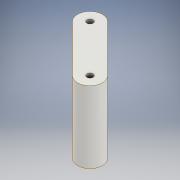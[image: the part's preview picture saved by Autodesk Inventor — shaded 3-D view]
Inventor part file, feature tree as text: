
AUTODESK INVENTOR PART (.ipt)
format: ipt  version: 2020 (Build 240168000, 168)  size: 368,128 bytes
history: native  units: mm
features: projected_geometry x10, other x4, extrude x1, sketch x1
ambient origin geometry x8: Origin, YZ Plane, XZ Plane, XY Plane, X Axis, Y Axis, Z Axis, Center Point
bodies: Body1 (feature_tree)
feature tree (16):
  other  "motor_converter.ipt"
  extrude  "Выдавливание1"  Depth=10.0mm
  other  "Твердое тело7::motor_converter.ipt"
  other  "Элемент создания тегов1"
  sketch  "Эскиз1"
  projected_geometry  "Спроецированная петля1"
  projected_geometry  "Спроецированная петля2"
  projected_geometry  "Спроецированная петля3"
  projected_geometry  "Спроецированная петля4"
  projected_geometry  "Спроецированная петля5"
  projected_geometry  "Спроецированная петля6"
  projected_geometry  "Спроецированная петля7"
  projected_geometry  "Спроецированная петля8"
  projected_geometry  "Спроецированная петля9"
  projected_geometry  "Спроецированная петля10"
  other  "Твердое тело1"
